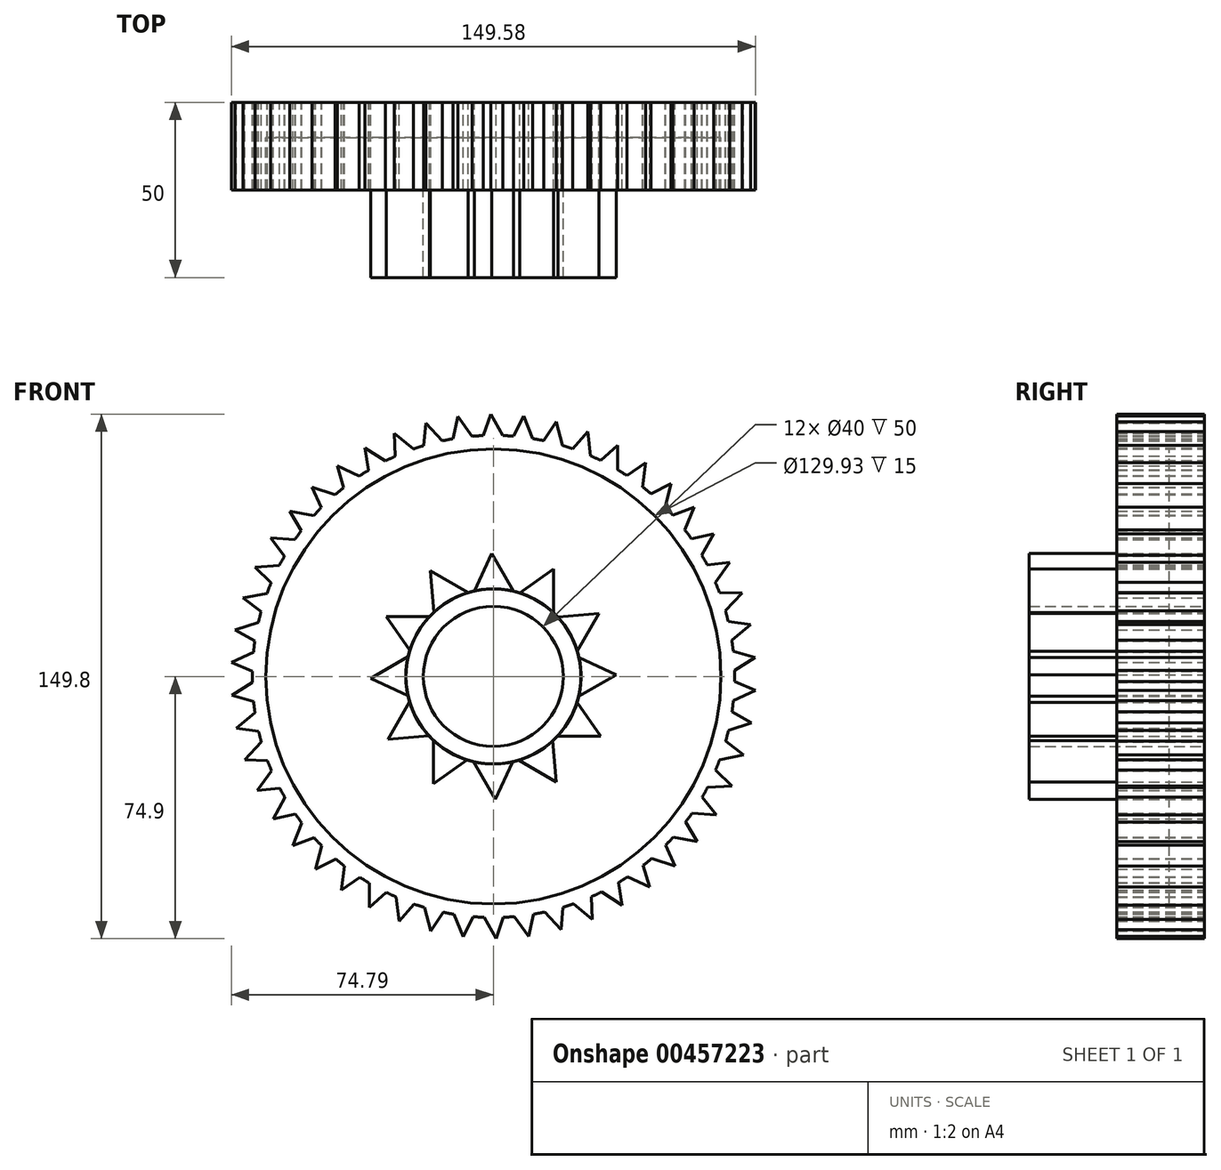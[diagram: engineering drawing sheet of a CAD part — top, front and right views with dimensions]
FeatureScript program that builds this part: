
annotation { "Feature Type Name" : "Feature", "Feature Type Description" : "" }
export const myFeature = defineFeature(function(context is Context, id is Id, definition is map)
    precondition{}
    {
        {
            var Q0;
            Q0=qCreatedBy(makeId("Front.planeOp"),FACE);
            var sketch = newSketch(context, id + "F0", { "sketchPlane" : qUnion([Q0])});
            skCircle(sketch, "E0", {"center": v(0, 0) * mm, "radius": 20 * mm});
            skCircle(sketch, "E1", {"center": v(0, 0) * mm, "radius": 25 * mm});
            skArc(sketch, "E2", {"start": v(7.47, 23.86) * mm, "mid": v(12.6, 21.6) * mm, "end": v(17.1, 18.23) * mm});
            skCircle(sketch, "E3", {"center": v(0, 0) * mm, "radius": 35.08 * mm, "construction": true});
            skLineSegment(sketch, "E4", {"start": v(7.47, 23.86) * mm, "end": v(17.1, 30.63) * mm});
            skLineSegment(sketch, "E5", {"start": v(17.1, 30.63) * mm, "end": v(17.1, 18.23) * mm});
            skSolve(sketch);
        }
        {
            var Q0;
            Q0=qCreatedBy(makeId("Front.planeOp"),FACE);
            var sketch = newSketch(context, id + "F1", { "sketchPlane" : qUnion([Q0])});
            skCircle(sketch, "E6", {"center": v(0, 0) * mm, "radius": 64.97 * mm});
            skCircle(sketch, "E7", {"center": v(0, 0) * mm, "radius": 68.84 * mm});
            skArc(sketch, "E8", {"start": v(30.62, 61.66) * mm, "mid": v(33.06, 60.39) * mm, "end": v(35.44, 59.02) * mm});
            skCircle(sketch, "E9", {"center": v(0, 0) * mm, "radius": 74.9 * mm, "construction": true});
            skLineSegment(sketch, "E10", {"start": v(30.62, 61.66) * mm, "end": v(35.44, 65.98) * mm});
            skLineSegment(sketch, "E11", {"start": v(35.44, 65.98) * mm, "end": v(35.44, 59.02) * mm});
            skSolve(sketch);
        }
        {
            var Q0;
            Q0=makeQuery(id+"F0.imprint","IMPRINT",FACE,{"disambiguationData":[TD([[makeQuery(id+"F0.imprint","IMPRINT",EDGE,{"derivedFrom":sQuery(id+"F0.wireOp",EDGE,"E0")}),-1.0]])]});
            extrude(context, id + "F2", {"entities" : qUnion([Q0]), "depth" : 50 * mm});
        }
        {
            var Q0;
            {var subQ0=sQuery(id+"F0.wireOp",EDGE,"E4");Q0=makeQuery(id+"F0.imprint","IMPRINT",FACE,{"disambiguationData":[TD([[makeQuery(id+"F0.imprint","IMPRINT",EDGE,{"derivedFrom":subQ0}),-1.0]])]});}
            extrude(context, id + "F3", {"entities" : qUnion([Q0]), "operationType" : NewBodyOperationType.ADD, "depth" : 50 * mm});
        }
        {
            var Q0;
            Q0=makeQuery(id+"F2.opExtrude","SWEPT_BODY",BODY,{"disambiguationData":[OSD([sQuery(id+"F0.wireOp",EDGE,"E0"),sQuery(id+"F0.wireOp",EDGE,"E1")])]});
            var Q1;
            Q1=sQuery(id+"F0.wireOp",EDGE,"E0");
            circularPattern(context, id + "F4", {"entities" : qUnion([Q0]), "axis" : qUnion([Q1]), "angle" : 360 * degree, "instanceCount" : 12, "equalSpace" : true});
        }
        {
            var Q0;
            Q0=makeQuery(id+"F1.imprint","IMPRINT",FACE,{"disambiguationData":[TD([[makeQuery(id+"F1.imprint","IMPRINT",EDGE,{"derivedFrom":sQuery(id+"F1.wireOp",EDGE,"E6")}),1.0]])]});
            extrude(context, id + "F5", {"entities" : qUnion([Q0]), "depth" : 10 * mm});
        }
        {
            var Q0;
            Q0=makeQuery(id+"F1.imprint","IMPRINT",FACE,{"disambiguationData":[TD([[makeQuery(id+"F1.imprint","IMPRINT",EDGE,{"derivedFrom":sQuery(id+"F1.wireOp",EDGE,"E6")}),-1.0]])]});
            var Q1;
            {var subQ0=sQuery(id+"F1.wireOp",EDGE,"E10");Q1=makeQuery(id+"F1.imprint","IMPRINT",FACE,{"disambiguationData":[TD([[makeQuery(id+"F1.imprint","IMPRINT",EDGE,{"derivedFrom":subQ0}),-1.0]])]});}
            extrude(context, id + "F6", {"entities" : qUnion([Q0, Q1]), "depth" : 25 * mm});
        }
        {
            var Q0;
            Q0=makeQuery(id+"F6.opExtrude","SWEPT_BODY",BODY,{"disambiguationData":[OSD([sQuery(id+"F1.wireOp",EDGE,"E6"),sQuery(id+"F1.wireOp",EDGE,"E7"),sQuery(id+"F1.wireOp",EDGE,"E10"),sQuery(id+"F1.wireOp",EDGE,"E11")])]});
            var Q1;
            Q1=makeQuery(id+"F2.opExtrude","CAP_EDGE",EDGE,{"disambiguationData":[OSD([sQuery(id+"F0.wireOp",EDGE,"E0")])],"isStart":false});
            circularPattern(context, id + "F7", {"operationType" : NewBodyOperationType.ADD, "entities" : qUnion([Q0]), "axis" : qUnion([Q1]), "angle" : 360 * degree, "instanceCount" : 50, "equalSpace" : true});
        }
    });
